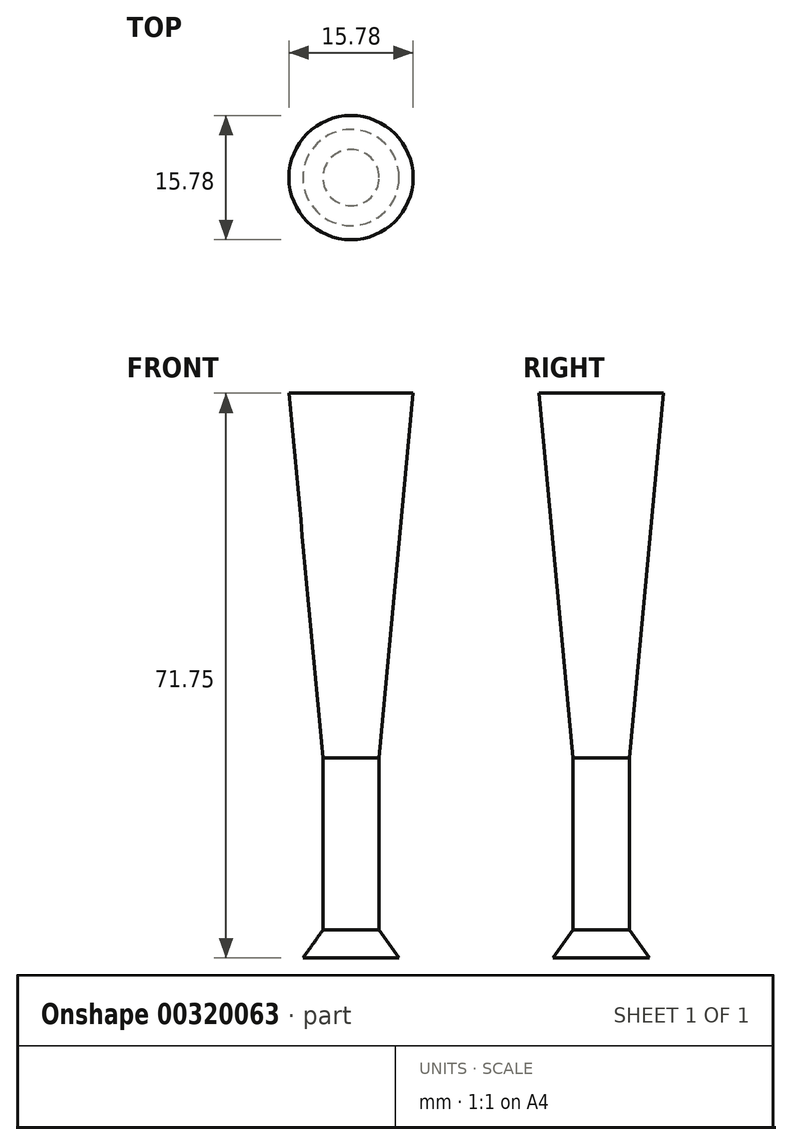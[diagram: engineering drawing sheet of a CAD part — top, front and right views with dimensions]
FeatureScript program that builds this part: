
annotation { "Feature Type Name" : "Feature", "Feature Type Description" : "" }
export const myFeature = defineFeature(function(context is Context, id is Id, definition is map)
    precondition{}
    {
        {
            var Q0;
            Q0=qCreatedBy(makeId("Front.planeOp"),FACE);
            var sketch = newSketch(context, id + "F0", { "sketchPlane" : qUnion([Q0])});
            skLineSegment(sketch, "E0", {"start": v(0, 43.38) * mm, "end": v(-7.89, 43.38) * mm});
            skLineSegment(sketch, "E1", {"start": v(-7.89, 43.38) * mm, "end": v(-3.56, -2.93) * mm});
            skLineSegment(sketch, "E2", {"start": v(-3.56, -2.93) * mm, "end": v(-3.56, -17.17) * mm});
            skLineSegment(sketch, "E3", {"start": v(-3.56, -17.17) * mm, "end": v(-3.56, -24.8) * mm});
            skLineSegment(sketch, "E4", {"start": v(-3.56, -24.8) * mm, "end": v(-6.1, -28.37) * mm});
            skLineSegment(sketch, "E5", {"start": v(-6.1, -28.37) * mm, "end": v(0, -28.37) * mm});
            skLineSegment(sketch, "E6", {"start": v(0, -28.37) * mm, "end": v(0, 43.38) * mm});
            skSolve(sketch);
        }
        {
            var Q0;
            Q0=makeQuery(id+"F0.imprint","IMPRINT",FACE,{"disambiguationData":[TD([[makeQuery(id+"F0.imprint","IMPRINT",EDGE,{"derivedFrom":sQuery(id+"F0.wireOp",EDGE,"E0")}),1.0]])]});
            var Q1;
            Q1=sQuery(id+"F0.wireOp",EDGE,"E6");
            revolve(context, id + "F1", {"entities" : qUnion([Q0]), "axis" : qUnion([Q1]), "revolveType" : RevolveType.FULL});
        }
    });
